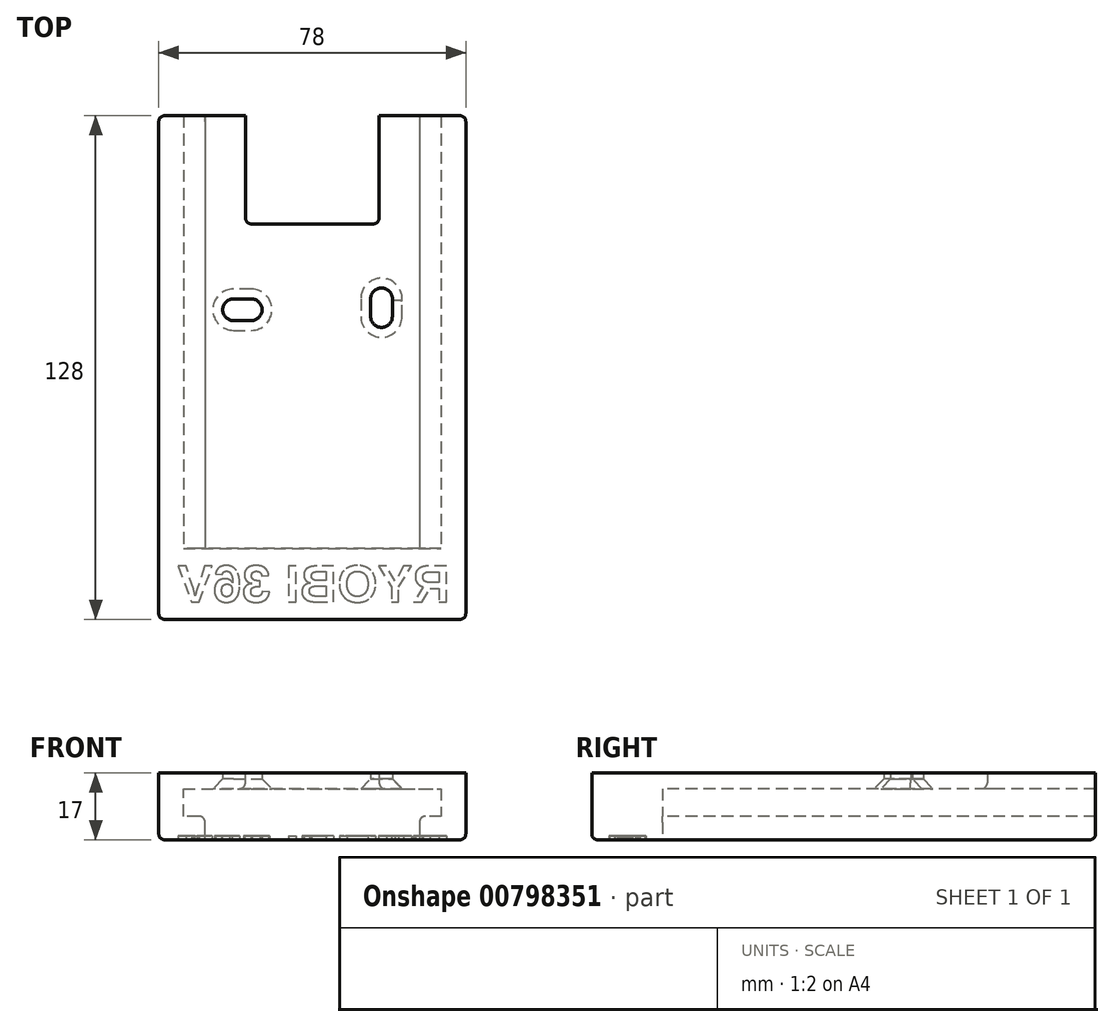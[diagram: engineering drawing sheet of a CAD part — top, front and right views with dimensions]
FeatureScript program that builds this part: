
annotation { "Feature Type Name" : "Feature", "Feature Type Description" : "" }
export const myFeature = defineFeature(function(context is Context, id is Id, definition is map)
    precondition{}
    {
        {
            var Q0;
            Q0=qCreatedBy(makeId("Top.planeOp"),FACE);
            var sketch = newSketch(context, id + "F0", { "sketchPlane" : qUnion([Q0])});
            skLineSegment(sketch, "E0.bottom", {"start": v(-39, 64) * mm, "end": v(39, 64) * mm});
            skLineSegment(sketch, "E0.top", {"start": v(-39, -64) * mm, "end": v(39, -64) * mm});
            skLineSegment(sketch, "E0.left", {"start": v(-39, 64) * mm, "end": v(-39, -64) * mm});
            skLineSegment(sketch, "E0.right", {"start": v(39, 64) * mm, "end": v(39, -64) * mm});
            skPoint(sketch, "E0.middle", {"position": v(0, 0) * mm});
            skLineSegment(sketch, "E1", {"start": v(-57.36, -46) * mm, "end": v(72.55, -46) * mm, "construction": true});
            skLineSegment(sketch, "E2", {"start": v(53.97, 36.5) * mm, "end": v(-60.96, 36.5) * mm, "construction": true});
            skSolve(sketch);
        }
        {
            var Q0;
            Q0 = qSketchRegion(id + "F0", true);
            extrude(context, id + "F1", {"entities" : qUnion([Q0]), "depth" : (12 + 5) * mm, "offsetDistance" : 25 * mm});
        }
        {
            var Q0;
            Q0=qCreatedBy(makeId("Front.planeOp"),FACE);
            var sketch = newSketch(context, id + "F2", { "sketchPlane" : qUnion([Q0])});
            skLineSegment(sketch, "E3", {"start": v(-27.25, 0) * mm, "end": v(-27.25, 6) * mm});
            skLineSegment(sketch, "E4", {"start": v(-27.25, 6) * mm, "end": v(-32.75, 6) * mm});
            skLineSegment(sketch, "E5", {"start": v(-32.75, 6) * mm, "end": v(-32.75, 13) * mm});
            skLineSegment(sketch, "E6", {"start": v(-32.75, 13) * mm, "end": v(32.75, 13) * mm});
            skLineSegment(sketch, "E7", {"start": v(32.75, 13) * mm, "end": v(32.75, 6) * mm});
            skLineSegment(sketch, "E8", {"start": v(32.75, 6) * mm, "end": v(27.25, 6) * mm});
            skLineSegment(sketch, "E9", {"start": v(27.25, 6) * mm, "end": v(27.25, 0) * mm});
            skLineSegment(sketch, "E10", {"start": v(27.25, 0) * mm, "end": v(-27.25, 0) * mm});
            skSolve(sketch);
        }
        {
            var Q0;
            Q0 = qSketchRegion(id + "F2", true);
            extrude(context, id + "F3", {"entities" : qUnion([Q0]), "operationType" : NewBodyOperationType.REMOVE, "endBound" : BoundingType.UP_TO_NEXT, "oppositeDirection" : true, "depth" : 25 * mm, "offsetDistance" : 25 * mm, "hasSecondDirection" : true, "secondDirectionOppositeDirection" : false, "secondDirectionDepth" : 46 * mm});
        }
        {
            var Q0;
            Q0=qCreatedBy(makeId("Top.planeOp"),FACE);
            var sketch = newSketch(context, id + "F4", { "sketchPlane" : qUnion([Q0])});
            skLineSegment(sketch, "E11", {"start": v(17, 36.5) * mm, "end": v(-17, 36.5) * mm});
            skLineSegment(sketch, "E12", {"start": v(-17, 36.5) * mm, "end": v(-17, 69.4) * mm});
            skLineSegment(sketch, "E13", {"start": v(-17, 69.4) * mm, "end": v(17, 69.4) * mm});
            skLineSegment(sketch, "E14", {"start": v(17, 69.4) * mm, "end": v(17, 36.5) * mm});
            skSolve(sketch);
        }
        {
            var Q0;
            Q0 = qSketchRegion(id + "F4", true);
            extrude(context, id + "F5", {"entities" : qUnion([Q0]), "operationType" : NewBodyOperationType.REMOVE, "endBound" : BoundingType.THROUGH_ALL, "depth" : 25 * mm, "offsetDistance" : 25 * mm});
        }
        {
            var Q0;
            Q0=qCreatedBy(makeId("Top.planeOp"),FACE);
            var sketch = newSketch(context, id + "F6", { "sketchPlane" : qUnion([Q0])});
            skLineSegment(sketch, "E15", {"start": v(14.83, 17.44) * mm, "end": v(14.83, 12.94) * mm});
            skLineSegment(sketch, "E16", {"start": v(20.33, 17.08) * mm, "end": v(20.33, 12.94) * mm});
            skArc(sketch, "E17", {"start": v(20.33, 12.94) * mm, "mid": v(17.58, 10.2) * mm, "end": v(14.83, 12.94) * mm});
            skArc(sketch, "E18", {"start": v(14.83, 17.44) * mm, "mid": v(17.77, 20.2) * mm, "end": v(20.33, 17.08) * mm});
            skLineSegment(sketch, "E19", {"start": v(-15.52, 17.44) * mm, "end": v(-20.02, 17.44) * mm});
            skLineSegment(sketch, "E20", {"start": v(-15.52, 11.94) * mm, "end": v(-20.02, 11.94) * mm});
            skArc(sketch, "E21", {"start": v(-20.02, 11.94) * mm, "mid": v(-22.77, 14.7) * mm, "end": v(-20.02, 17.44) * mm});
            skArc(sketch, "E22", {"start": v(-15.52, 17.44) * mm, "mid": v(-12.77, 14.7) * mm, "end": v(-15.52, 11.94) * mm});
            skLineSegment(sketch, "E23", {"start": v(-17.5, 35.87) * mm, "end": v(-17.5, -10.95) * mm, "construction": true});
            skLineSegment(sketch, "E24", {"start": v(17.5, 35.87) * mm, "end": v(17.5, -10.95) * mm, "construction": true});
            skLineSegment(sketch, "E25", {"start": v(-42.1, 15) * mm, "end": v(26.43, 15) * mm, "construction": true});
            skSolve(sketch);
        }
        {
            var Q0;
            Q0 = qSketchRegion(id + "F6", true);
            extrude(context, id + "F7", {"entities" : qUnion([Q0]), "operationType" : NewBodyOperationType.REMOVE, "endBound" : BoundingType.THROUGH_ALL, "depth" : 25 * mm, "offsetDistance" : 25 * mm});
        }
        {
            var Q0;
            Q0=makeQuery(id+"F7.boolean.opBoolean","INTERSECT",EDGE,{"derivedFrom":[makeQuery(id+"F3.boolean.opBoolean","COPY",FACE,{"derivedFrom":makeQuery(id+"F3.opExtrude","SWEPT_FACE",FACE,{"disambiguationData":[OSD([sQuery(id+"F2.wireOp",EDGE,"E6")])]})}),makeQuery(id+"F7.opExtrude","SWEPT_FACE",FACE,{"disambiguationData":[OSD([sQuery(id+"F6.wireOp",EDGE,"E18")])]})]});
            var Q1;
            Q1=makeQuery(id+"F7.boolean.opBoolean","INTERSECT",EDGE,{"derivedFrom":[makeQuery(id+"F3.boolean.opBoolean","COPY",FACE,{"derivedFrom":makeQuery(id+"F3.opExtrude","SWEPT_FACE",FACE,{"disambiguationData":[OSD([sQuery(id+"F2.wireOp",EDGE,"E6")])]})}),makeQuery(id+"F7.opExtrude","SWEPT_FACE",FACE,{"disambiguationData":[OSD([sQuery(id+"F6.wireOp",EDGE,"E22")])]})]});
            chamfer(context, id + "F8", {"entities" : qUnion([Q0, Q1]), "width" : 2.5 * mm, "tangentPropagation" : true});
        }
        {
            var Q0;
            Q0=makeQuery(id+"F5.boolean.opBoolean","INTERSECT",EDGE,{"derivedFrom":[makeQuery(id+"F3.boolean.opBoolean","COPY",FACE,{"derivedFrom":makeQuery(id+"F3.opExtrude","SWEPT_FACE",FACE,{"disambiguationData":[OSD([sQuery(id+"F2.wireOp",EDGE,"E6")])]})}),makeQuery(id+"F5.opExtrude","SWEPT_FACE",FACE,{"disambiguationData":[OSD([sQuery(id+"F4.wireOp",EDGE,"E12")])]})]});
            var Q1;
            Q1=makeQuery(id+"F5.boolean.opBoolean","INTERSECT",EDGE,{"derivedFrom":[makeQuery(id+"F3.boolean.opBoolean","COPY",FACE,{"derivedFrom":makeQuery(id+"F3.opExtrude","SWEPT_FACE",FACE,{"disambiguationData":[OSD([sQuery(id+"F2.wireOp",EDGE,"E6")])]})}),makeQuery(id+"F5.opExtrude","SWEPT_FACE",FACE,{"disambiguationData":[OSD([sQuery(id+"F4.wireOp",EDGE,"E11")])]})]});
            var Q2;
            Q2=makeQuery(id+"F5.boolean.opBoolean","INTERSECT",EDGE,{"derivedFrom":[makeQuery(id+"F3.boolean.opBoolean","COPY",FACE,{"derivedFrom":makeQuery(id+"F3.opExtrude","SWEPT_FACE",FACE,{"disambiguationData":[OSD([sQuery(id+"F2.wireOp",EDGE,"E6")])]})}),makeQuery(id+"F5.opExtrude","SWEPT_FACE",FACE,{"disambiguationData":[OSD([sQuery(id+"F4.wireOp",EDGE,"E14")])]})]});
            var Q3;
            {var subQ0=sQuery(id+"F2.wireOp",EDGE,"E6");Q3=makeQuery(id+"F5.boolean.opBoolean","SPLIT",EDGE,{"disambiguationData":[TD([makeQuery(id+"F3.boolean.opBoolean","COPY",FACE,{"derivedFrom":makeQuery(id+"F3.opExtrude","SWEPT_FACE",FACE,{"disambiguationData":[OSD([sQuery(id+"F2.wireOp",EDGE,"E5")])]})})])],"derivedFrom":makeQuery(id+"F3.boolean.opBoolean","COPY",EDGE,{"derivedFrom":makeQuery(id+"F3.opExtrude","CAP_EDGE",EDGE,{"disambiguationData":[OSD([subQ0])],"isStart":false})})});}
            var Q4;
            {var subQ0=sQuery(id+"F2.wireOp",EDGE,"E6");Q4=makeQuery(id+"F5.boolean.opBoolean","SPLIT",EDGE,{"disambiguationData":[TD([makeQuery(id+"F3.boolean.opBoolean","COPY",FACE,{"derivedFrom":makeQuery(id+"F3.opExtrude","SWEPT_FACE",FACE,{"disambiguationData":[OSD([sQuery(id+"F2.wireOp",EDGE,"E7")])]})})])],"derivedFrom":makeQuery(id+"F3.boolean.opBoolean","COPY",EDGE,{"derivedFrom":makeQuery(id+"F3.opExtrude","CAP_EDGE",EDGE,{"disambiguationData":[OSD([subQ0])],"isStart":false})})});}
            var Q5;
            Q5=makeQuery(id+"F3.boolean.opBoolean","COPY",EDGE,{"derivedFrom":makeQuery(id+"F3.opExtrude","CAP_EDGE",EDGE,{"disambiguationData":[OSD([sQuery(id+"F2.wireOp",EDGE,"E7")])],"isStart":false})});
            var Q6;
            Q6=makeQuery(id+"F3.boolean.opBoolean","COPY",EDGE,{"derivedFrom":makeQuery(id+"F3.opExtrude","CAP_EDGE",EDGE,{"disambiguationData":[OSD([sQuery(id+"F2.wireOp",EDGE,"E8")])],"isStart":false})});
            var Q7;
            Q7=makeQuery(id+"F3.boolean.opBoolean","COPY",EDGE,{"derivedFrom":makeQuery(id+"F3.opExtrude","CAP_EDGE",EDGE,{"disambiguationData":[OSD([sQuery(id+"F2.wireOp",EDGE,"E5")])],"isStart":false})});
            var Q8;
            Q8=makeQuery(id+"F3.boolean.opBoolean","COPY",EDGE,{"derivedFrom":makeQuery(id+"F3.opExtrude","CAP_EDGE",EDGE,{"disambiguationData":[OSD([sQuery(id+"F2.wireOp",EDGE,"E4")])],"isStart":false})});
            var Q9;
            Q9=makeQuery(id+"F3.boolean.opBoolean","COPY",EDGE,{"derivedFrom":makeQuery(id+"F3.opExtrude","SWEPT_EDGE",EDGE,{"disambiguationData":[OSD([sQuery(id+"F2.wireOp",EDGE,"E3"),sQuery(id+"F2.wireOp",EDGE,"E4")])]})});
            var Q10;
            Q10=makeQuery(id+"F3.boolean.opBoolean","COPY",EDGE,{"derivedFrom":makeQuery(id+"F3.opExtrude","SWEPT_EDGE",EDGE,{"disambiguationData":[OSD([sQuery(id+"F2.wireOp",EDGE,"E8"),sQuery(id+"F2.wireOp",EDGE,"E9")])]})});
            var Q11;
            Q11=makeQuery(id+"F3.boolean.opBoolean","COPY",EDGE,{"derivedFrom":makeQuery(id+"F3.opExtrude","SWEPT_EDGE",EDGE,{"disambiguationData":[OSD([sQuery(id+"F2.wireOp",EDGE,"E9"),sQuery(id+"F2.wireOp",EDGE,"E10")])]})});
            var Q12;
            Q12=makeQuery(id+"F3.boolean.opBoolean","COPY",EDGE,{"derivedFrom":makeQuery(id+"F3.opExtrude","SWEPT_EDGE",EDGE,{"disambiguationData":[OSD([sQuery(id+"F2.wireOp",EDGE,"E3"),sQuery(id+"F2.wireOp",EDGE,"E10")])]})});
            var Q13;
            Q13=makeQuery(id+"F3.boolean.opBoolean","COPY",EDGE,{"derivedFrom":makeQuery(id+"F3.opExtrude","CAP_EDGE",EDGE,{"disambiguationData":[OSD([sQuery(id+"F2.wireOp",EDGE,"E10")])],"isStart":true})});
            var Q14;
            Q14=makeQuery(id+"F1.opExtrude","CAP_EDGE",EDGE,{"disambiguationData":[OSD([sQuery(id+"F0.wireOp",EDGE,"E0.right")])],"isStart":true});
            var Q15;
            Q15=makeQuery(id+"F1.opExtrude","CAP_EDGE",EDGE,{"disambiguationData":[OSD([sQuery(id+"F0.wireOp",EDGE,"E0.left")])],"isStart":true});
            var Q16;
            Q16=makeQuery(id+"F1.opExtrude","CAP_EDGE",EDGE,{"disambiguationData":[OSD([sQuery(id+"F0.wireOp",EDGE,"E0.top")])],"isStart":true});
            var Q17;
            {var subQ0=sQuery(id+"F0.wireOp",EDGE,"E0.bottom");var subQ1=sQuery(id+"F0.wireOp",EDGE,"E0.left");Q17=makeQuery(id+"F3.boolean.opBoolean","SPLIT",EDGE,{"disambiguationData":[TD([makeQuery(id+"F1.opExtrude","SWEPT_FACE",FACE,{"disambiguationData":[OSD([subQ1])]})])],"derivedFrom":makeQuery(id+"F1.opExtrude","CAP_EDGE",EDGE,{"disambiguationData":[OSD([subQ0])],"isStart":true})});}
            var Q18;
            {var subQ0=sQuery(id+"F0.wireOp",EDGE,"E0.bottom");var subQ1=sQuery(id+"F0.wireOp",EDGE,"E0.right");Q18=makeQuery(id+"F3.boolean.opBoolean","SPLIT",EDGE,{"disambiguationData":[TD([makeQuery(id+"F1.opExtrude","SWEPT_FACE",FACE,{"disambiguationData":[OSD([subQ1])]})])],"derivedFrom":makeQuery(id+"F1.opExtrude","CAP_EDGE",EDGE,{"disambiguationData":[OSD([subQ0])],"isStart":true})});}
            var Q19;
            Q19=makeQuery(id+"F1.opExtrude","SWEPT_EDGE",EDGE,{"disambiguationData":[OSD([sQuery(id+"F0.wireOp",EDGE,"E0.top"),sQuery(id+"F0.wireOp",EDGE,"E0.right")])]});
            var Q20;
            Q20=makeQuery(id+"F1.opExtrude","SWEPT_EDGE",EDGE,{"disambiguationData":[OSD([sQuery(id+"F0.wireOp",EDGE,"E0.top"),sQuery(id+"F0.wireOp",EDGE,"E0.left")])]});
            var Q21;
            Q21=makeQuery(id+"F1.opExtrude","SWEPT_EDGE",EDGE,{"disambiguationData":[OSD([sQuery(id+"F0.wireOp",EDGE,"E0.bottom"),sQuery(id+"F0.wireOp",EDGE,"E0.left")])]});
            var Q22;
            Q22=makeQuery(id+"F1.opExtrude","SWEPT_EDGE",EDGE,{"disambiguationData":[OSD([sQuery(id+"F0.wireOp",EDGE,"E0.bottom"),sQuery(id+"F0.wireOp",EDGE,"E0.right")])]});
            var Q23;
            Q23=makeQuery(id+"F5.boolean.opBoolean","COPY",EDGE,{"derivedFrom":makeQuery(id+"F5.opExtrude","SWEPT_EDGE",EDGE,{"disambiguationData":[OSD([sQuery(id+"F4.wireOp",EDGE,"E11"),sQuery(id+"F4.wireOp",EDGE,"E12")])]})});
            var Q24;
            Q24=makeQuery(id+"F5.boolean.opBoolean","COPY",EDGE,{"derivedFrom":makeQuery(id+"F5.opExtrude","SWEPT_EDGE",EDGE,{"disambiguationData":[OSD([sQuery(id+"F4.wireOp",EDGE,"E11"),sQuery(id+"F4.wireOp",EDGE,"E14")])]})});
            fillet(context, id + "F9", {"entities" : qUnion([Q0, Q1, Q2, Q3, Q4, Q5, Q6, Q7, Q8, Q9, Q10, Q11, Q12, Q13, Q14, Q15, Q16, Q17, Q18, Q19, Q20, Q21, Q22, Q23, Q24]), "radius" : 1.5 * mm, "tangentPropagation" : true, "allowEdgeOverflow" : false});
        }
        {
            var Q0;
            Q0=makeQuery(id+"F1.opExtrude","CAP_FACE",FACE,{"disambiguationData":[OSD([sQuery(id+"F0.wireOp",EDGE,"E0.bottom"),sQuery(id+"F0.wireOp",EDGE,"E0.top"),sQuery(id+"F0.wireOp",EDGE,"E0.left"),sQuery(id+"F0.wireOp",EDGE,"E0.right")])],"isStart":true});
            var sketch = newSketch(context, id + "F10", { "sketchPlane" : qUnion([Q0])});
            skText(sketch, "E26", { "text": "RYOBI 36V", "fontName": "Arimo-Bold.ttf"});
            const initialGuessF10  = {"E26": [0.035, 0.05953, -1, 0, 0.00953]};
            skSetInitialGuess(sketch, initialGuessF10);
            skSolve(sketch);
        }
        {
            var Q0;
            Q0 = qSketchRegion(id + "F10", true);
            extrude(context, id + "F11", {"entities" : qUnion([Q0]), "operationType" : NewBodyOperationType.REMOVE, "oppositeDirection" : true, "depth" : 1 * mm, "offsetDistance" : 25 * mm});
        }
    });
